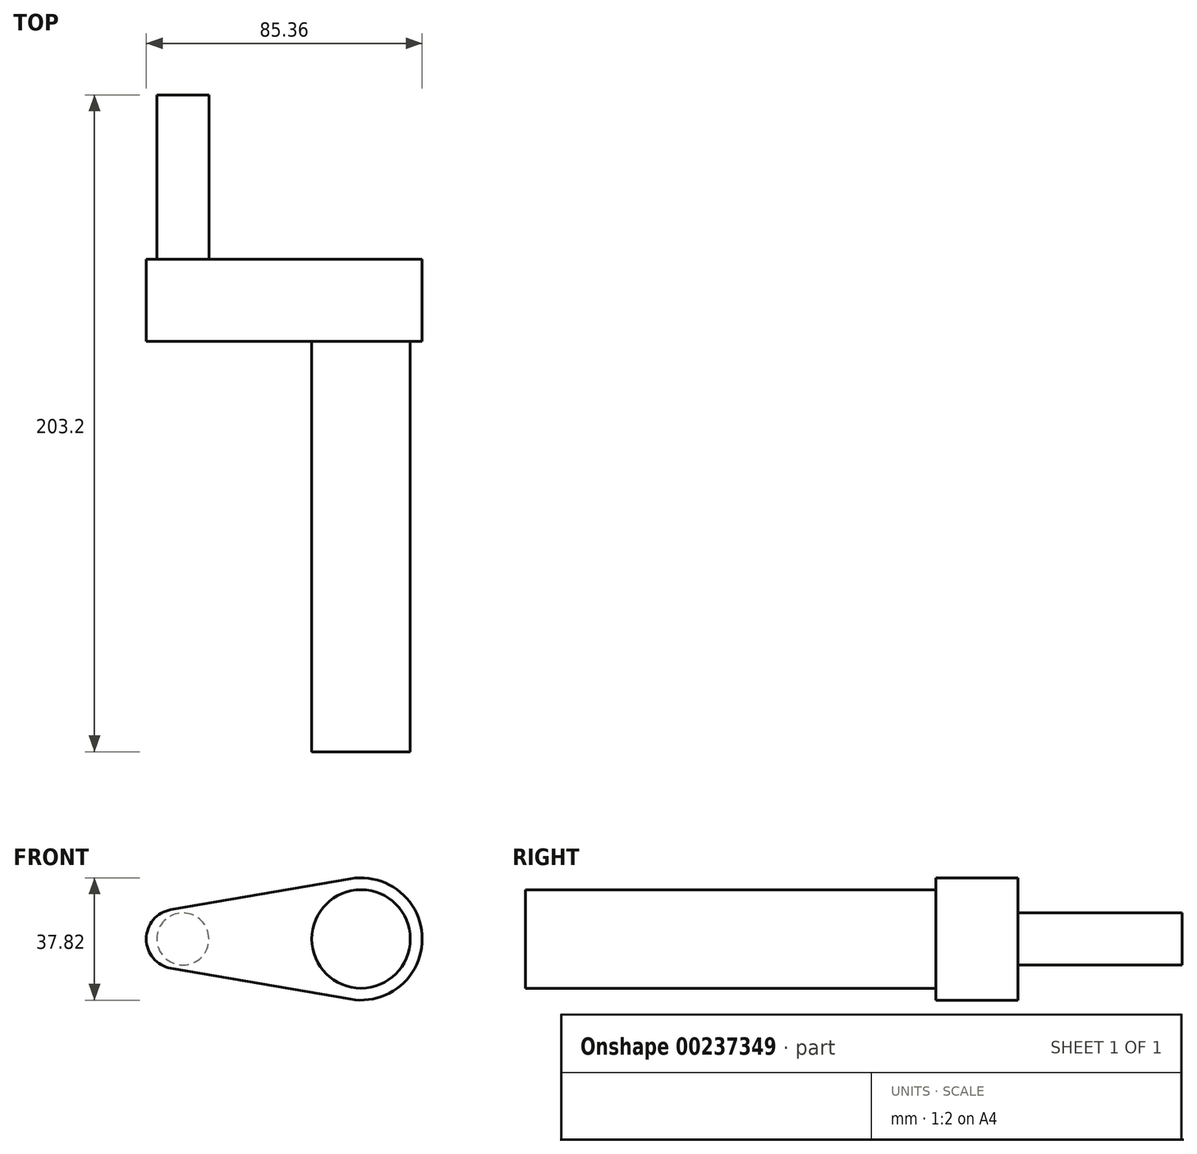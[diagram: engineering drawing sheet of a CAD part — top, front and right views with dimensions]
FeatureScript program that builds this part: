
annotation { "Feature Type Name" : "Feature", "Feature Type Description" : "" }
export const myFeature = defineFeature(function(context is Context, id is Id, definition is map)
    precondition{}
    {
        {
            var Q0;
            Q0=qCreatedBy(makeId("Front.planeOp"),FACE);
            var sketch = newSketch(context, id + "F0", { "sketchPlane" : qUnion([Q0])});
            skCircle(sketch, "E0", {"center": v(0, 0) * mm, "radius": 15.24 * mm});
            skSolve(sketch);
        }
        {
            var Q0;
            Q0 = qSketchRegion(id + "F0", true);
            extrude(context, id + "F1", {"entities" : qUnion([Q0]), "depth" : 152.4 * mm});
        }
        {
            var Q0;
            Q0=qCreatedBy(makeId("Front.planeOp"),FACE);
            var sketch = newSketch(context, id + "F2", { "sketchPlane" : qUnion([Q0])});
            skArc(sketch, "E1", {"start": v(-3.2, -18.64) * mm, "mid": v(18.91, 0) * mm, "end": v(-3.2, 18.64) * mm});
            skArc(sketch, "E2", {"start": v(-58.81, 9.07) * mm, "mid": v(-66.45, 0) * mm, "end": v(-58.81, -9.07) * mm});
            skLineSegment(sketch, "E3", {"start": v(-3.2, 18.64) * mm, "end": v(-58.81, 9.07) * mm});
            skLineSegment(sketch, "E4", {"start": v(-3.2, -18.64) * mm, "end": v(-58.81, -9.07) * mm});
            skSolve(sketch);
        }
        {
            var Q0;
            Q0 = qSketchRegion(id + "F2", true);
            extrude(context, id + "F3", {"entities" : qUnion([Q0]), "operationType" : NewBodyOperationType.ADD, "depth" : 25.4 * mm});
        }
        {
            var Q0;
            Q0=qCreatedBy(makeId("Front.planeOp"),FACE);
            var sketch = newSketch(context, id + "F4", { "sketchPlane" : qUnion([Q0])});
            skCircle(sketch, "E5", {"center": v(-55.14, 0) * mm, "radius": 8.06 * mm});
            skSolve(sketch);
        }
        {
            var Q0;
            Q0=makeQuery(id+"F4.imprint","IMPRINT",FACE,{"disambiguationData":[TD([[makeQuery(id+"F4.imprint","IMPRINT",EDGE,{"derivedFrom":sQuery(id+"F4.wireOp",EDGE,"E5")}),1.0]])]});
            extrude(context, id + "F5", {"entities" : qUnion([Q0]), "operationType" : NewBodyOperationType.ADD, "oppositeDirection" : true, "depth" : 50.8 * mm});
        }
    });
